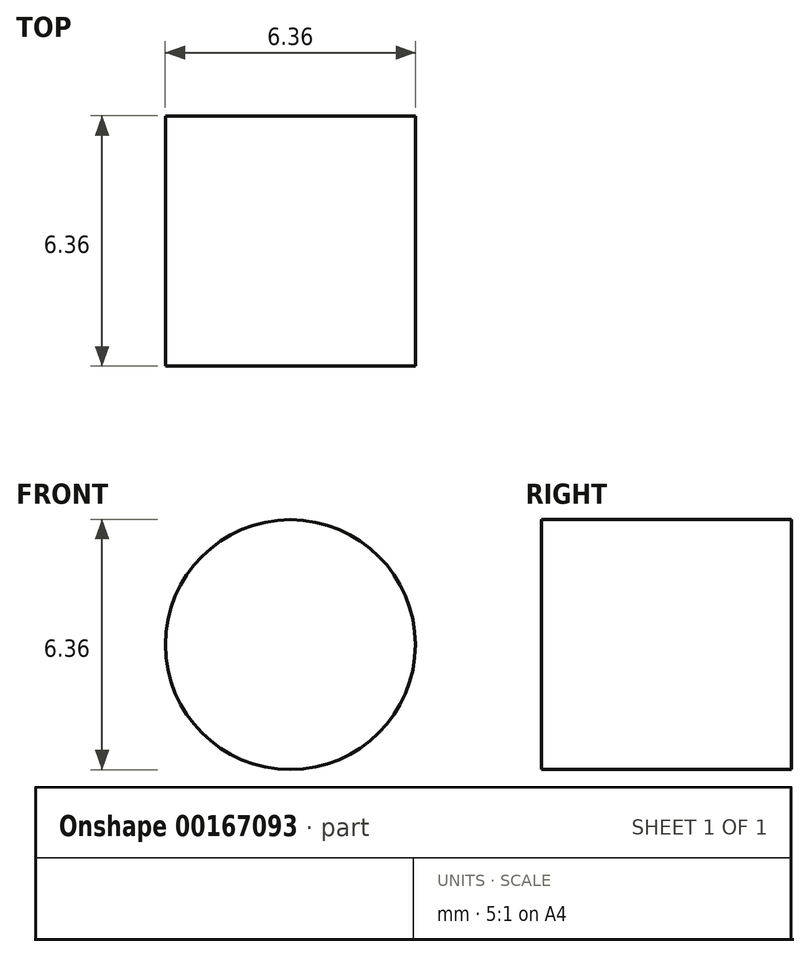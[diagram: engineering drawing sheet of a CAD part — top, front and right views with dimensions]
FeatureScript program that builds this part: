
annotation { "Feature Type Name" : "Feature", "Feature Type Description" : "" }
export const myFeature = defineFeature(function(context is Context, id is Id, definition is map)
    precondition{}
    {
        {
            var Q0;
            Q0=qCreatedBy(makeId("Front.planeOp"),FACE);
            var sketch = newSketch(context, id + "F0", { "sketchPlane" : qUnion([Q0])});
            skCircle(sketch, "E0", {"center": v(0, 0) * mm, "radius": 3.18 * mm});
            skSolve(sketch);
        }
        {
            var Q0;
            Q0 = qSketchRegion(id + "F0", true);
            extrude(context, id + "F1", {"entities" : qUnion([Q0]), "endBound" : BoundingType.SYMMETRIC, "depth" : 6.35 * mm});
        }
    });
